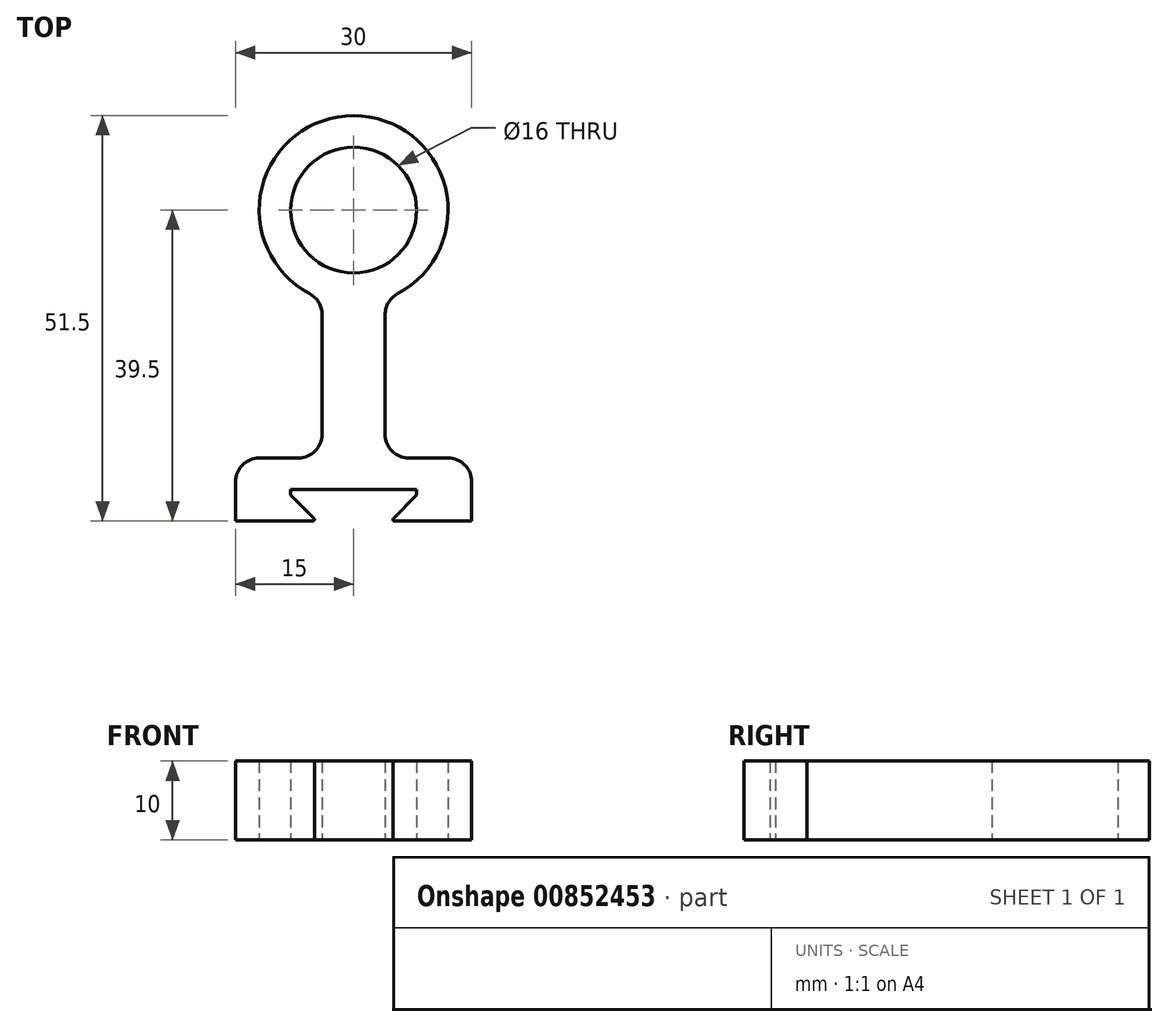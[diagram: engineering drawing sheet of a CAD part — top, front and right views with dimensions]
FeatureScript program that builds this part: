
annotation { "Feature Type Name" : "Feature", "Feature Type Description" : "" }
export const myFeature = defineFeature(function(context is Context, id is Id, definition is map)
    precondition{}
    {
        {
            var Q0;
            Q0=qCreatedBy(makeId("Top.planeOp"),FACE);
            var sketch = newSketch(context, id + "F0", { "sketchPlane" : qUnion([Q0])});
            skLineSegment(sketch, "E0.right", {"start": v(15, 1) * mm, "end": v(15, -4) * mm});
            skLineSegment(sketch, "E1.top", {"start": v(7, 4) * mm, "end": v(12, 4) * mm});
            skLineSegment(sketch, "E2", {"start": v(0, 41.18) * mm, "end": v(0, -31.23) * mm, "construction": true});
            skLineSegment(sketch, "E3", {"start": v(-15, 1) * mm, "end": v(-15, -4) * mm});
            skLineSegment(sketch, "E4", {"start": v(-15, -4) * mm, "end": v(-5.18, -4) * mm});
            skLineSegment(sketch, "E5.MirrorCS", {"start": v(15, -4) * mm, "end": v(5.18, -4) * mm});
            skLineSegment(sketch, "E6", {"start": v(-5.04, -3.66) * mm, "end": v(-8, -0.7) * mm});
            skLineSegment(sketch, "E7", {"start": v(-8, -0.7) * mm, "end": v(-8, 0) * mm});
            skLineSegment(sketch, "E8.MirrorCS", {"start": v(5.04, -3.66) * mm, "end": v(8, -0.7) * mm});
            skLineSegment(sketch, "E9.MirrorCS", {"start": v(8, -0.7) * mm, "end": v(8, 0) * mm});
            skLineSegment(sketch, "E10", {"start": v(-8, 0) * mm, "end": v(8, 0) * mm});
            skPoint(sketch, "E11.visualSharp", {"position": v(-4.7, -4) * mm});
            skArc(sketch, "E11.filletArc", {"start": v(-5.18, -4) * mm, "mid": v(-5, -3.88) * mm, "end": v(-5.04, -3.66) * mm});
            skPoint(sketch, "E12.visualSharp", {"position": v(4.7, -4) * mm});
            skArc(sketch, "E12.filletArc", {"start": v(5.04, -3.66) * mm, "mid": v(5, -3.88) * mm, "end": v(5.18, -4) * mm});
            skLineSegment(sketch, "E13.left", {"start": v(-4, 7) * mm, "end": v(-4, 22.23) * mm});
            skLineSegment(sketch, "E13.right", {"start": v(4, 7) * mm, "end": v(4, 22.23) * mm});
            skArc(sketch, "E14", {"start": v(5.6, 24.89) * mm, "mid": v(0, 47.5) * mm, "end": v(-5.6, 24.89) * mm});
            skCircle(sketch, "E15", {"center": v(0, 35.5) * mm, "radius": 8 * mm});
            skPoint(sketch, "E16.visualSharp", {"position": v(-15, 4) * mm});
            skArc(sketch, "E16.filletArc", {"start": v(-12, 4) * mm, "mid": v(-14.12, 3.12) * mm, "end": v(-15, 1) * mm});
            skPoint(sketch, "E17.visualSharp", {"position": v(15, 4) * mm});
            skArc(sketch, "E17.filletArc", {"start": v(15, 1) * mm, "mid": v(14.12, 3.12) * mm, "end": v(12, 4) * mm});
            skPoint(sketch, "E18.newPointA", {"position": v(4, 5.69) * mm});
            skArc(sketch, "E18.filletArc", {"start": v(4, 7) * mm, "mid": v(4.88, 4.88) * mm, "end": v(7, 4) * mm});
            skLineSegment(sketch, "E19", {"start": v(-7, 4) * mm, "end": v(-12, 4) * mm});
            skPoint(sketch, "E20.visualSharp", {"position": v(-4, 4) * mm});
            skArc(sketch, "E20.filletArc", {"start": v(-7, 4) * mm, "mid": v(-4.88, 4.88) * mm, "end": v(-4, 7) * mm});
            skPoint(sketch, "E21.visualSharp", {"position": v(-4, 24.19) * mm});
            skArc(sketch, "E21.filletArc", {"start": v(-4, 22.23) * mm, "mid": v(-4.43, 23.78) * mm, "end": v(-5.6, 24.89) * mm});
            skPoint(sketch, "E22.visualSharp", {"position": v(4, 24.19) * mm});
            skArc(sketch, "E22.filletArc", {"start": v(5.6, 24.89) * mm, "mid": v(4.43, 23.78) * mm, "end": v(4, 22.23) * mm});
            skSolve(sketch);
        }
        {
            var Q0;
            Q0=qSketchRegion(id+"F0",true);
            extrude(context, id + "F1", {"entities" : qUnion([Q0]), "depth" : 10 * mm, "offsetDistance" : 25 * mm, "symmetric" : true});
        }
    });
